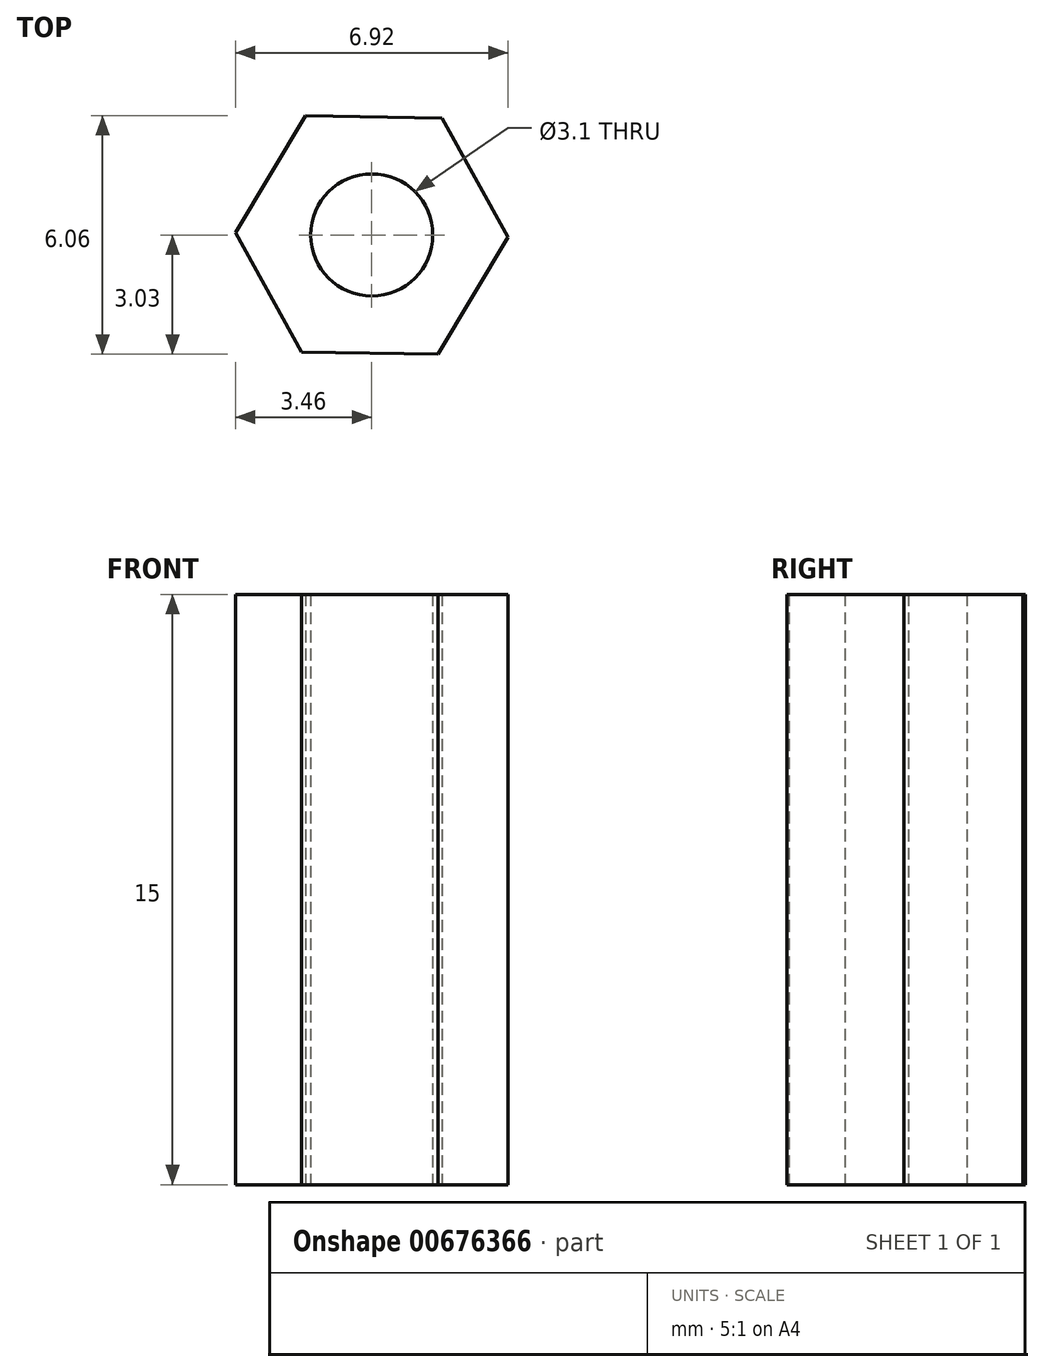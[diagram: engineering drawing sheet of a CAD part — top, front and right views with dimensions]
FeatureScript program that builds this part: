
annotation { "Feature Type Name" : "Feature", "Feature Type Description" : "" }
export const myFeature = defineFeature(function(context is Context, id is Id, definition is map)
    precondition{}
    {
        {
            var Q0;
            Q0=qCreatedBy(makeId("Top.planeOp"),FACE);
            var sketch = newSketch(context, id + "F0", { "sketchPlane" : qUnion([Q0])});
            skCircle(sketch, "E0.cCircle", {"center": v(0, 0) * mm, "radius": 3 * mm, "construction": true});
            skLineSegment(sketch, "E0.0", {"start": v(3.46, -0.06) * mm, "end": v(1.68, -3.03) * mm});
            skLineSegment(sketch, "E0.1", {"start": v(1.68, -3.03) * mm, "end": v(-1.78, -2.97) * mm});
            skLineSegment(sketch, "E0.2", {"start": v(-1.78, -2.97) * mm, "end": v(-3.46, 0.06) * mm});
            skLineSegment(sketch, "E0.3", {"start": v(-3.46, 0.06) * mm, "end": v(-1.68, 3.03) * mm});
            skLineSegment(sketch, "E0.4", {"start": v(-1.68, 3.03) * mm, "end": v(1.78, 2.97) * mm});
            skLineSegment(sketch, "E0.5", {"start": v(1.78, 2.97) * mm, "end": v(3.46, -0.06) * mm});
            skPoint(sketch, "E0.0.midPoint", {"position": v(2.57, -1.54) * mm});
            skCircle(sketch, "E1", {"center": v(0, 0) * mm, "radius": 1.55 * mm});
            skSolve(sketch);
        }
        {
            var Q0;
            Q0 = qSketchRegion(id + "F0", true);
            extrude(context, id + "F1", {"entities" : qUnion([Q0]), "depth" : 15 * mm, "offsetDistance" : 25 * mm});
        }
    });
